# Revit family: OF-TxXPx
name_source: partatom
category: Furniture
units: mm (PartAtom-declared; Revit-internal decimal feet)

## family parameters
Always vertical = Yes
Cut with Voids When Loaded = No
Room Calculation Point = No
Shared = No
Work Plane-Based = No

## types (9) — shared parameters
Default Elevation = 0' - 0"

## per-type parameters (varying)
| type | Bench Width | ES Seat Count | HS Seat Count | In Ground | Leg Placement | Mount | Surface Mount | Table Width |
| OF-T6XPP | 6' - 0" | 8 | 6 | No | 3' - 10 1/8" | No | No | 6' - 0" |
| OF-T8XPP | 8' - 0" | 12 | 8 | No | 5' - 10 1/8" | No | No | 8' - 0" |
| OF-T8XPP-ADA | 6' - 0" | 8 | 6 | No | 3' - 10 1/8" | No | No | 8' - 0" |
| OF-T6XPSM | 6' - 0" | 8 | 6 | No | 3' - 10 1/8" | Yes | Yes | 6' - 0" |
| OF-T6XPIG | 6' - 0" | 8 | 6 | Yes | 3' - 10 1/8" | Yes | No | 6' - 0" |
| OF-T8XPSM | 8' - 0" | 12 | 8 | No | 5' - 10 1/8" | Yes | Yes | 8' - 0" |
| OF-T8XPIG | 8' - 0" | 12 | 8 | Yes | 5' - 10 1/8" | Yes | No | 8' - 0" |
| OF-T8XPSM-ADA | 6' - 0" | 8 | 6 | No | 3' - 10 1/8" | Yes | Yes | 8' - 0" |
| OF-T8XPIG-ADA | 6' - 0" | 8 | 6 | Yes | 3' - 10 1/8" | Yes | No | 8' - 0" |

note: column(s) folded — value = type name in every type: Model

## geometry (parser evidence)
native form markers: Sweep x3
no freeform markers — native parametric forms only
